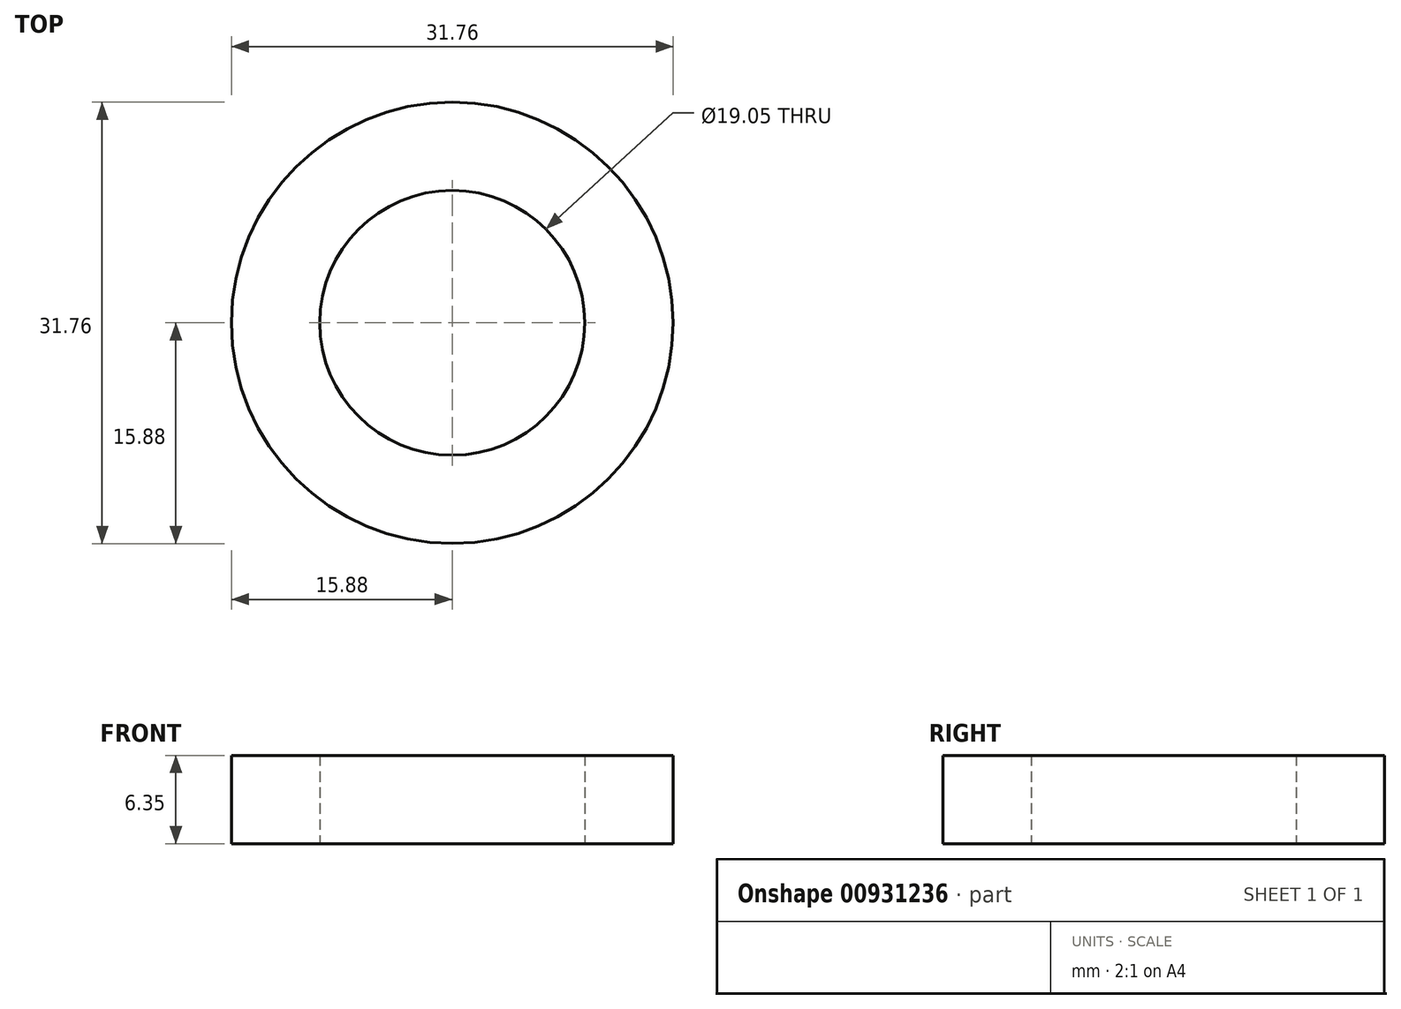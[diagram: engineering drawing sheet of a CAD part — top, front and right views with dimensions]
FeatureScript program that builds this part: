
annotation { "Feature Type Name" : "Feature", "Feature Type Description" : "" }
export const myFeature = defineFeature(function(context is Context, id is Id, definition is map)
    precondition{}
    {
        {
            var Q0;
            Q0=qCreatedBy(makeId("Top.planeOp"),FACE);
            var sketch = newSketch(context, id + "F0", { "sketchPlane" : qUnion([Q0])});
            skCircle(sketch, "E0", {"center": v(0, 0) * mm, "radius": 9.53 * mm});
            skCircle(sketch, "E1.0", {"center": v(0, 0) * mm, "radius": 15.88 * mm});
            skSolve(sketch);
        }
        {
            var Q0;
            Q0 = qSketchRegion(id + "F0", true);
            extrude(context, id + "F1", {"entities" : qUnion([Q0]), "depth" : 6.35 * mm, "offsetDistance" : 25.4 * mm});
        }
    });
